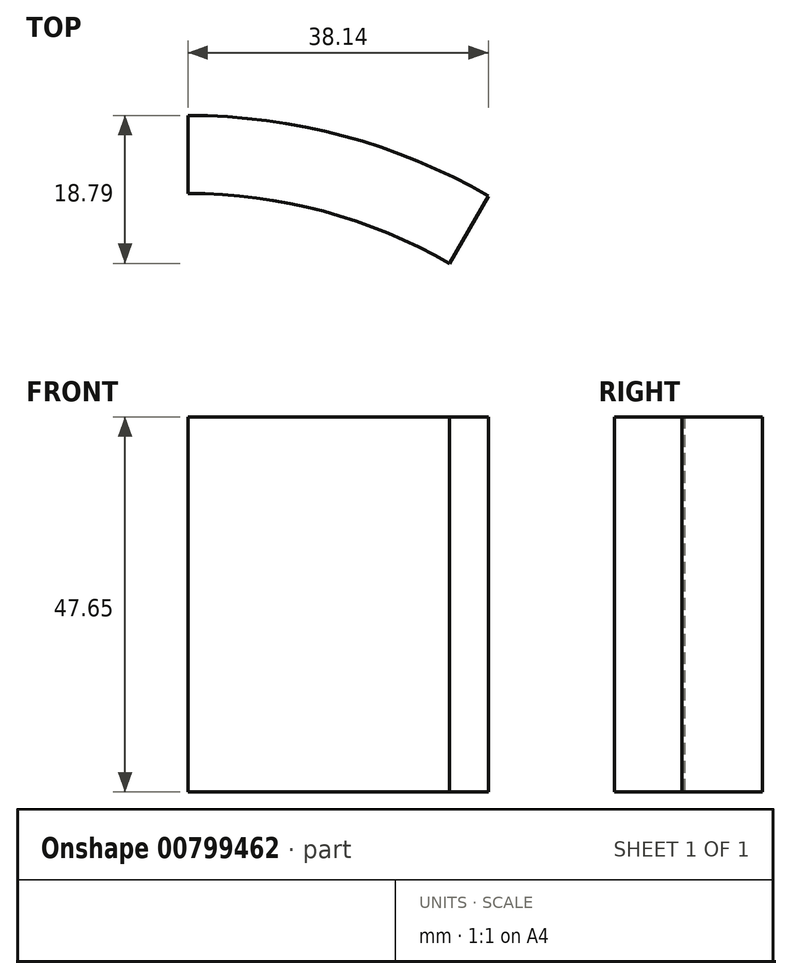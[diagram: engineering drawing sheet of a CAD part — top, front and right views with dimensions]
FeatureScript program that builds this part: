
annotation { "Feature Type Name" : "Feature", "Feature Type Description" : "" }
export const myFeature = defineFeature(function(context is Context, id is Id, definition is map)
    precondition{}
    {
        {
            var Q0;
            Q0=qCreatedBy(makeId("Front.planeOp"),FACE);
            var sketch = newSketch(context, id + "F0", { "sketchPlane" : qUnion([Q0])});
            skLineSegment(sketch, "E0", {"start": v(0, 33.73) * mm, "end": v(0, -33.1) * mm});
            skSolve(sketch);
        }
        {
            var Q0;
            Q0=qCreatedBy(makeId("Right.planeOp"),FACE);
            var sketch = newSketch(context, id + "F1", { "sketchPlane" : qUnion([Q0])});
            skLineSegment(sketch, "E1", {"start": v(66.37, 39.3) * mm, "end": v(66.37, -40.54) * mm});
            skLineSegment(sketch, "E2", {"start": v(66.37, -40.54) * mm, "end": v(0, -40.54) * mm});
            skLineSegment(sketch, "E3", {"start": v(60.8, 38.68) * mm, "end": v(60.8, -34.97) * mm});
            skLineSegment(sketch, "E4", {"start": v(60.8, -34.97) * mm, "end": v(0, -34.97) * mm});
            skLineSegment(sketch, "E5", {"start": v(60.8, 38.68) * mm, "end": v(66.37, 39.3) * mm});
            skLineSegment(sketch, "E6", {"start": v(0, -40.54) * mm, "end": v(0, -34.97) * mm});
            skLineSegment(sketch, "E7", {"start": v(0, 26.3) * mm, "end": v(53.38, 26.3) * mm});
            skLineSegment(sketch, "E8", {"start": v(53.38, 26.3) * mm, "end": v(76.27, 26.3) * mm});
            skLineSegment(sketch, "E9", {"start": v(76.27, 26.3) * mm, "end": v(76.27, -21.35) * mm});
            skLineSegment(sketch, "E10", {"start": v(76.27, -21.35) * mm, "end": v(0, -21.35) * mm});
            skSolve(sketch);
        }
        {
            var Q0;
            {var subQ5=sQuery(id+"F1.wireOp",EDGE,"E9");Q0=makeQuery(id+"F1.imprint","IMPRINT",FACE,{"disambiguationData":[TD([[makeQuery(id+"F1.imprint","IMPRINT",EDGE,{"derivedFrom":subQ5}),-1.0]])]});}
            var Q1;
            Q1=sQuery(id+"F0.wireOp",EDGE,"E0");
            revolve(context, id + "F2", {"surfaceOperationType" : NewSurfaceOperationType.NEW, "entities" : qUnion([Q0]), "axis" : qUnion([Q1]), "revolveType" : RevolveType.ONE_DIRECTION, "angle" : 30 * degree});
        }
    });
